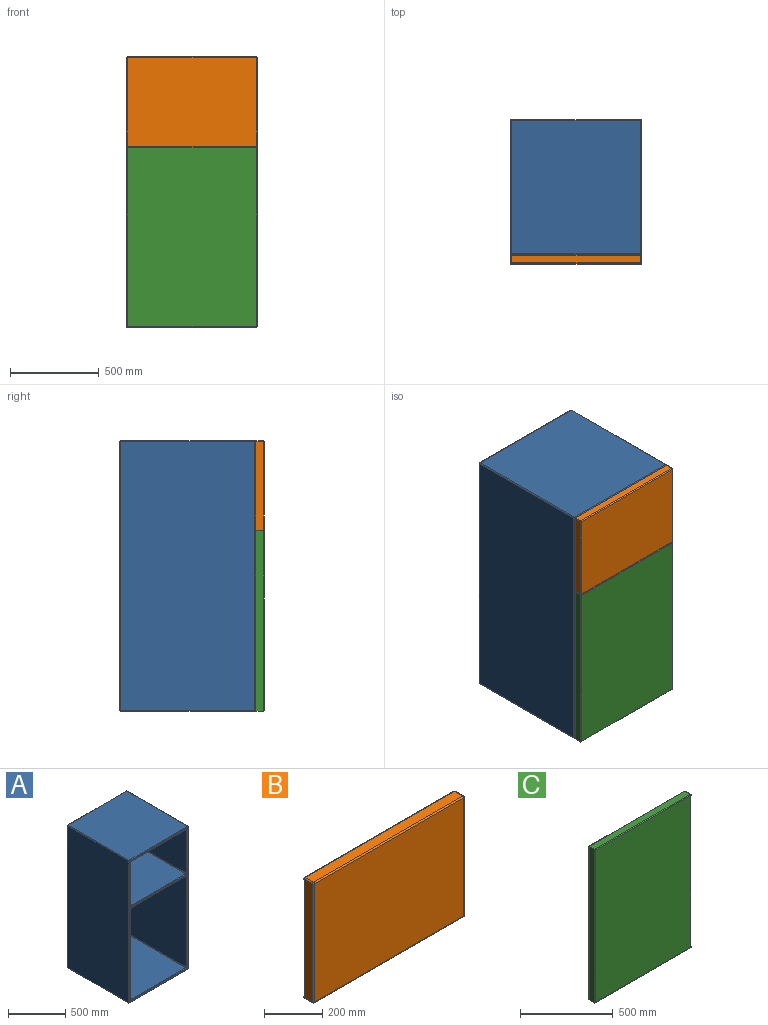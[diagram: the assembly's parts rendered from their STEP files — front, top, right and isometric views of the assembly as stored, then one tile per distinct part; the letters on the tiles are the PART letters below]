
ASSEMBLY  parts=3 mates=2
PART A: 73 faces, bbox 736.6x762x1524 mm
  f0: plane 1513.84x731.52mm, normal (0,-1,0), area 85828.7mm2, adj f6,f16,f17,f18,f19,f23,f24,f25
  f1: plane 967.74x675.64mm, normal (0,-1,0), area 653843.9mm2, adj f21,f30,f31,f35
  f2: plane 726.44x459.74mm, normal (1,0,0), area 333973.5mm2, adj f39,f40,f49,f50
  f3: plane 726.44x459.74mm, normal (-1,0,0), area 333973.5mm2, adj f42,f43,f51,f52
  f4: plane 1513.84x726.44mm, normal (0,1,0), area 1099713.9mm2, adj f61,f66,f69,f72
  f5: plane 1513.84x751.84mm, normal (-1,0,0), area 1138165.5mm2, adj f58,f67,f68,f72
  f6: plane 1513.84x756.92mm, normal (1,0,0), area 1145855.8mm2, adj f0,f56,f60,f61
  f7: plane 751.84x726.44mm, normal (0,0,1), area 546166.6mm2, adj f56,f57,f66,f67
  f8: plane 751.84x726.44mm, normal (0,0,-1), area 546166.6mm2, adj f59,f60,f68,f69
  f9: plane 675.64x459.74mm, normal (0,-1,0), area 310618.7mm2, adj f41,f50,f51,f55
  f10: plane 967.74x726.44mm, normal (1,0,0), area 703005mm2, adj f24,f29,f32,f35
  f11: plane 967.74x726.44mm, normal (-1,0,0), area 703005mm2, adj f16,f20,f21,f22
  f12: plane 726.44x675.64mm, normal (0,0,-1), area 490811.9mm2, adj f36,f40,f41,f42
  f13: plane 726.44x675.64mm, normal (0,0,1), area 490811.9mm2, adj f22,f23,f31,f32
  f14: plane 726.44x675.64mm, normal (0,0,1), area 490811.9mm2, adj f44,f49,f52,f55
  f15: plane 726.44x675.64mm, normal (0,0,-1), area 490811.9mm2, adj f19,f20,f29,f30
  f16: cylinder r=5.08mm len=967.74mm, axis (0,0,1), area 7722.2mm2, adj f0,f11,f17,f18
  f17: torus R=10.16mm, axis (0,1,0), area 86.8mm2, adj f0,f16,f19,f20
  f18: torus R=10.16mm, axis (0,1,0), area 86.8mm2, adj f0,f16,f22,f23
  f19: cylinder r=5.08mm len=675.64mm, axis (-1,0,0), area 5391.4mm2, adj f0,f15,f17,f25
  f20: cylinder r=5.08mm len=726.44mm, axis (0,1,0), area 5796.7mm2, adj f11,f15,f17,f26
  f21: cylinder r=5.08mm len=967.74mm, axis (0,0,-1), area 7722.2mm2, adj f1,f11,f26,f27
  f22: cylinder r=5.08mm len=726.44mm, axis (0,-1,0), area 5796.7mm2, adj f11,f13,f18,f27
  f23: cylinder r=5.08mm len=675.64mm, axis (-1,0,0), area 5391.4mm2, adj f0,f13,f18,f28
  f24: cylinder r=5.08mm len=967.74mm, axis (0,0,-1), area 7722.2mm2, adj f0,f10,f25,f28
  f25: torus R=10.16mm, axis (0,1,0), area 86.8mm2, adj f0,f19,f24,f29
  f26: sphere r=5.08mm, area 40.5mm2, adj f20,f21,f30
  f27: sphere r=5.08mm, area 40.5mm2, adj f21,f22,f31
  f28: torus R=10.16mm, axis (0,1,0), area 86.8mm2, adj f0,f23,f24,f32
  f29: cylinder r=5.08mm len=726.44mm, axis (0,-1,0), area 5796.7mm2, adj f10,f15,f25,f33
  f30: cylinder r=5.08mm len=675.64mm, axis (1,0,0), area 5391.4mm2, adj f1,f15,f26,f33
  f31: cylinder r=5.08mm len=675.64mm, axis (1,0,0), area 5391.4mm2, adj f1,f13,f27,f34
  f32: cylinder r=5.08mm len=726.44mm, axis (0,1,0), area 5796.7mm2, adj f10,f13,f28,f34
  f33: sphere r=5.08mm, area 40.5mm2, adj f29,f30,f35
  f34: sphere r=5.08mm, area 40.5mm2, adj f31,f32,f35
  f35: cylinder r=5.08mm len=967.74mm, axis (0,0,1), area 7722.2mm2, adj f1,f10,f33,f34
  f36: cylinder r=5.08mm len=675.64mm, axis (1,0,0), area 5391.4mm2, adj f0,f12,f37,f38
  f37: torus R=10.16mm, axis (0,1,0), area 86.8mm2, adj f0,f36,f39,f40
  f38: torus R=10.16mm, axis (0,1,0), area 86.8mm2, adj f0,f36,f42,f43
  f39: cylinder r=5.08mm len=459.74mm, axis (0,0,-1), area 3668.6mm2, adj f0,f2,f37,f45
  f40: cylinder r=5.08mm len=726.44mm, axis (0,-1,0), area 5796.7mm2, adj f2,f12,f37,f46
  f41: cylinder r=5.08mm len=675.64mm, axis (-1,0,0), area 5391.4mm2, adj f9,f12,f46,f47
  f42: cylinder r=5.08mm len=726.44mm, axis (0,1,0), area 5796.7mm2, adj f3,f12,f38,f47
  f43: cylinder r=5.08mm len=459.74mm, axis (0,0,1), area 3668.6mm2, adj f0,f3,f38,f48
  f44: cylinder r=5.08mm len=675.64mm, axis (1,0,0), area 5391.4mm2, adj f0,f14,f45,f48
  f45: torus R=10.16mm, axis (0,1,0), area 86.8mm2, adj f0,f39,f44,f49
  f46: sphere r=5.08mm, area 40.5mm2, adj f40,f41,f50
  f47: sphere r=5.08mm, area 40.5mm2, adj f41,f42,f51
  f48: torus R=10.16mm, axis (0,1,0), area 86.8mm2, adj f0,f43,f44,f52
  f49: cylinder r=5.08mm len=726.44mm, axis (0,1,0), area 5796.7mm2, adj f2,f14,f45,f53
  f50: cylinder r=5.08mm len=459.74mm, axis (0,0,1), area 3668.6mm2, adj f2,f9,f46,f53
  f51: cylinder r=5.08mm len=459.74mm, axis (0,0,-1), area 3668.6mm2, adj f3,f9,f47,f54
  f52: cylinder r=5.08mm len=726.44mm, axis (0,-1,0), area 5796.7mm2, adj f3,f14,f48,f54
  f53: sphere r=5.08mm, area 40.5mm2, adj f49,f50,f55
  f54: sphere r=5.08mm, area 40.5mm2, adj f51,f52,f55
  f55: cylinder r=5.08mm len=675.64mm, axis (-1,0,0), area 5391.4mm2, adj f9,f14,f53,f54
  f56: cylinder r=5.08mm len=756.92mm, axis (0,-1,0), area 6025.2mm2, adj f6,f7,f57,f62
  f57: cylinder r=5.08mm len=731.52mm, axis (-1,0,0), area 5822.5mm2, adj f0,f7,f56,f63
  f58: cylinder r=5.08mm len=1513.84mm, axis (0,0,1), area 12079.9mm2, adj f0,f5,f63,f64
  f59: cylinder r=5.08mm len=731.52mm, axis (1,0,0), area 5822.5mm2, adj f0,f8,f60,f64
  f60: cylinder r=5.08mm len=756.92mm, axis (0,1,0), area 6025.2mm2, adj f6,f8,f59,f65
  f61: cylinder r=5.08mm len=1513.84mm, axis (0,0,1), area 12079.9mm2, adj f4,f6,f62,f65
  f62: sphere r=5.08mm, area 40.5mm2, adj f56,f61,f66
  f63: sphere r=5.08mm, area 40.5mm2, adj f57,f58,f67
  f64: sphere r=5.08mm, area 40.5mm2, adj f58,f59,f68
  f65: sphere r=5.08mm, area 40.5mm2, adj f60,f61,f69
  f66: cylinder r=5.08mm len=726.44mm, axis (1,0,0), area 5796.7mm2, adj f4,f7,f62,f70
  f67: cylinder r=5.08mm len=751.84mm, axis (0,1,0), area 5999.4mm2, adj f5,f7,f63,f70
  f68: cylinder r=5.08mm len=751.84mm, axis (0,-1,0), area 5999.4mm2, adj f5,f8,f64,f71
  f69: cylinder r=5.08mm len=726.44mm, axis (-1,0,0), area 5796.7mm2, adj f4,f8,f65,f71
  f70: sphere r=5.08mm, area 40.5mm2, adj f66,f67,f72
  f71: sphere r=5.08mm, area 40.5mm2, adj f68,f69,f72
  f72: cylinder r=5.08mm len=1513.84mm, axis (0,0,-1), area 12079.9mm2, adj f4,f5,f70,f71
PART B: 26 faces, bbox 736.6x50.8x508 mm
  f0: plane 497.84x40.64mm, normal (-1,0,0), area 20232.2mm2, adj f14,f19,f22,f25
  f1: plane 726.44x40.64mm, normal (0,0,-1), area 29522.5mm2, adj f11,f20,f21,f25
  f2: plane 497.84x40.64mm, normal (1,0,0), area 20232.2mm2, adj f6,f10,f11,f12
  f3: plane 726.44x40.64mm, normal (0,0,1), area 29522.5mm2, adj f6,f9,f13,f14
  f4: plane 726.44x497.84mm, normal (0,-1,0), area 361650.9mm2, adj f9,f10,f19,f20
  f5: plane 726.44x497.84mm, normal (0,1,0), area 361650.9mm2, adj f12,f13,f21,f22
  f6: cylinder r=5.08mm len=40.64mm, axis (0,1,0), area 324.3mm2, adj f2,f3,f7,f8
  f7: sphere r=5.08mm, area 40.5mm2, adj f6,f9,f10
  f8: sphere r=5.08mm, area 40.5mm2, adj f6,f12,f13
  f9: cylinder r=5.08mm len=726.44mm, axis (1,0,0), area 5796.7mm2, adj f3,f4,f7,f15
  f10: cylinder r=5.08mm len=497.84mm, axis (0,0,-1), area 3972.6mm2, adj f2,f4,f7,f16
  f11: cylinder r=5.08mm len=40.64mm, axis (0,-1,0), area 324.3mm2, adj f1,f2,f16,f17
  f12: cylinder r=5.08mm len=497.84mm, axis (0,0,1), area 3972.6mm2, adj f2,f5,f8,f17
  f13: cylinder r=5.08mm len=726.44mm, axis (-1,0,0), area 5796.7mm2, adj f3,f5,f8,f18
  f14: cylinder r=5.08mm len=40.64mm, axis (0,-1,0), area 324.3mm2, adj f0,f3,f15,f18
  f15: sphere r=5.08mm, area 40.5mm2, adj f9,f14,f19
  f16: sphere r=5.08mm, area 40.5mm2, adj f10,f11,f20
  f17: sphere r=5.08mm, area 40.5mm2, adj f11,f12,f21
  f18: sphere r=5.08mm, area 40.5mm2, adj f13,f14,f22
  f19: cylinder r=5.08mm len=497.84mm, axis (0,0,1), area 3972.6mm2, adj f0,f4,f15,f23
  f20: cylinder r=5.08mm len=726.44mm, axis (-1,0,0), area 5796.7mm2, adj f1,f4,f16,f23
  f21: cylinder r=5.08mm len=726.44mm, axis (1,0,0), area 5796.7mm2, adj f1,f5,f17,f24
  f22: cylinder r=5.08mm len=497.84mm, axis (0,0,-1), area 3972.6mm2, adj f0,f5,f18,f24
  f23: sphere r=5.08mm, area 40.5mm2, adj f19,f20,f25
  f24: sphere r=5.08mm, area 40.5mm2, adj f21,f22,f25
  f25: cylinder r=5.08mm len=40.64mm, axis (0,1,0), area 324.3mm2, adj f0,f1,f23,f24
PART C: 20 faces, bbox 736.6x50.8x1016 mm
  f0: plane 731.52x40.64mm, normal (0,0,1), area 29729mm2, adj f1,f6,f11,f16
  f1: plane 1016x40.64mm, normal (-1,0,0), area 41290.2mm2, adj f0,f2,f7,f17
  f2: plane 731.52x40.64mm, normal (0,0,-1), area 29729mm2, adj f1,f9,f14,f18
  f3: plane 1005.84x40.64mm, normal (1,0,0), area 40877.3mm2, adj f10,f11,f13,f14
  f4: plane 1005.84x726.44mm, normal (0,-1,0), area 730682.4mm2, adj f6,f7,f9,f10
  f5: plane 1005.84x726.44mm, normal (0,1,0), area 730682.4mm2, adj f13,f16,f17,f18
  f6: cylinder r=5.08mm len=731.52mm, axis (1,0,0), area 5822.5mm2, adj f0,f4,f7,f8
  f7: cylinder r=5.08mm len=1016mm, axis (0,0,1), area 8077.9mm2, adj f1,f4,f6,f9
  f8: sphere r=5.08mm, area 40.5mm2, adj f6,f10,f11
  f9: cylinder r=5.08mm len=731.52mm, axis (-1,0,0), area 5822.5mm2, adj f2,f4,f7,f12
  f10: cylinder r=5.08mm len=1005.84mm, axis (0,0,-1), area 8026.2mm2, adj f3,f4,f8,f12
  f11: cylinder r=5.08mm len=40.64mm, axis (0,1,0), area 324.3mm2, adj f0,f3,f8,f15
  f12: sphere r=5.08mm, area 40.5mm2, adj f9,f10,f14
  f13: cylinder r=5.08mm len=1005.84mm, axis (0,0,1), area 8026.2mm2, adj f3,f5,f15,f19
  f14: cylinder r=5.08mm len=40.64mm, axis (0,-1,0), area 324.3mm2, adj f2,f3,f12,f19
  f15: sphere r=5.08mm, area 40.5mm2, adj f11,f13,f16
  f16: cylinder r=5.08mm len=731.52mm, axis (-1,0,0), area 5822.5mm2, adj f0,f5,f15,f17
  f17: cylinder r=5.08mm len=1016mm, axis (0,0,-1), area 8077.9mm2, adj f1,f5,f16,f18
  f18: cylinder r=5.08mm len=731.52mm, axis (1,0,0), area 5822.5mm2, adj f2,f5,f17,f19
  f19: sphere r=5.08mm, area 40.5mm2, adj f13,f14,f18
PLACE A t=(-622.08,-12.83,-52.02)mm fixed
PLACE B t=(-622.08,-12.83,-52.02)mm
PLACE C t=(-622.08,-12.83,-52.02)mm
MATE fastened C.f5 <-> A.f68  axis (0,1,0) through (-617,-12.83,-46.94)mm
MATE fastened A.f67 <-> B.f14  axis (0,-1,0) through (-617,-12.83,1466.9)mm
